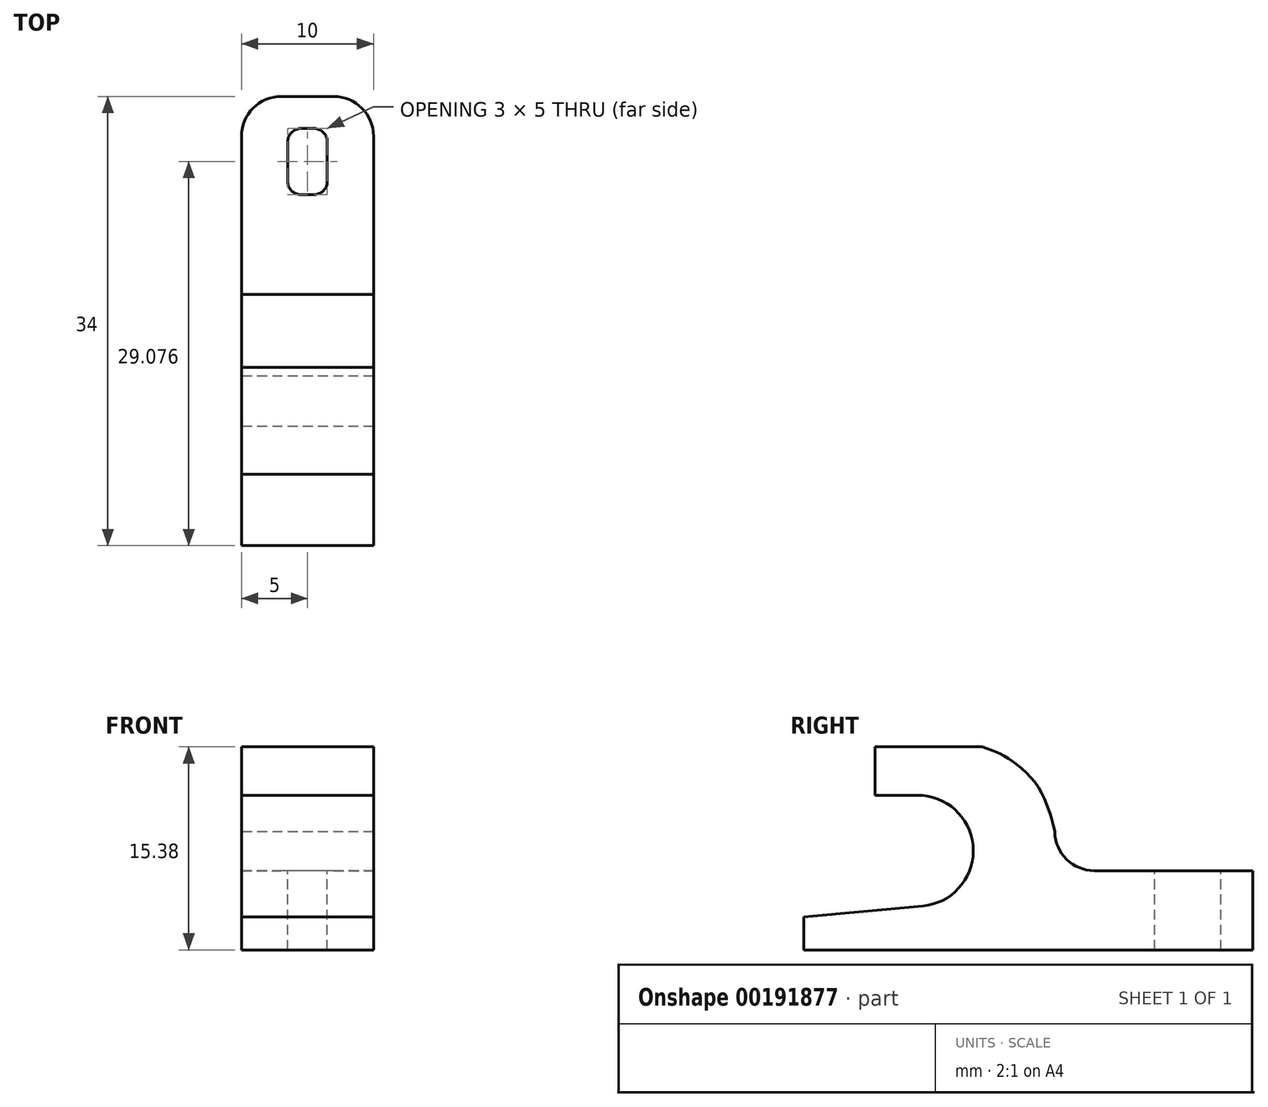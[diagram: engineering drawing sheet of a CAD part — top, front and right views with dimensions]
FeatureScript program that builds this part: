
annotation { "Feature Type Name" : "Feature", "Feature Type Description" : "" }
export const myFeature = defineFeature(function(context is Context, id is Id, definition is map)
    precondition{}
    {
        {
            var Q0;
            Q0=qCreatedBy(makeId("Right.planeOp"),FACE);
            var sketch = newSketch(context, id + "F0", { "sketchPlane" : qUnion([Q0])});
            skLineSegment(sketch, "E0", {"start": v(0, 0) * mm, "end": v(34, 0) * mm});
            skLineSegment(sketch, "E1", {"start": v(34, 0) * mm, "end": v(34, 6) * mm});
            skLineSegment(sketch, "E2", {"start": v(34, 6) * mm, "end": v(19, 6) * mm});
            skLineSegment(sketch, "E3", {"start": v(19, 6) * mm, "end": v(19, 8.93) * mm});
            skLineSegment(sketch, "E4", {"start": v(0, 2.5) * mm, "end": v(0, 0) * mm});
            skLineSegment(sketch, "E5", {"start": v(0, 2.5) * mm, "end": v(9, 3.32) * mm});
            skArc(sketch, "E6", {"start": v(9, 3.32) * mm, "mid": v(12.83, 7.5) * mm, "end": v(9, 11.7) * mm});
            skLineSegment(sketch, "E7", {"start": v(9, 11.7) * mm, "end": v(5.4, 11.7) * mm});
            skLineSegment(sketch, "E8", {"start": v(5.4, 11.7) * mm, "end": v(5.4, 13.28) * mm});
            skLineSegment(sketch, "E9", {"start": v(5.4, 13.28) * mm, "end": v(5.4, 15.38) * mm});
            skLineSegment(sketch, "E10", {"start": v(5.4, 15.38) * mm, "end": v(13.5, 15.38) * mm});
            skFitSpline(sketch, "E11", {"points": [v(13.5, 15.38) * mm, v(15.35, 14.6) * mm, v(17.58, 12.58) * mm, v(18.76, 9.98) * mm, v(19, 8.93) * mm, v(19.4, 7.6) * mm, v(20.08, 8.62) * mm, v(20.9, 12) * mm, v(21.25, 17.14) * mm, v(15.66, 18.14) * mm, v(13.29, 16.85) * mm, v(13.45, 16.25) * mm, v(11.41, 16.25) * mm, v(13.5, 15.38) * mm]});
            skPoint(sketch, "E12.start.orphan", {"position": v(19, 15.38) * mm});
            skPoint(sketch, "E13.orphan", {"position": v(19, 13.28) * mm});
            skPoint(sketch, "E14.end.orphan", {"position": v(9, 13.28) * mm});
            skSolve(sketch);
        }
        {
            var Q0;
            Q0=makeQuery(id+"F0.imprint","IMPRINT",FACE,{"disambiguationData":[TD([[makeQuery(id+"F0.imprint","IMPRINT",EDGE,{"derivedFrom":sQuery(id+"F0.wireOp",EDGE,"E0")}),1.0]])]});
            extrude(context, id + "F1", {"entities" : qUnion([Q0]), "depth" : 10 * mm});
        }
        {
            var Q0;
            Q0=makeQuery(id+"F1.opExtrude","SWEPT_EDGE",EDGE,{"disambiguationData":[OSD([sQuery(id+"F0.wireOp",EDGE,"E2"),sQuery(id+"F0.wireOp",EDGE,"E3")])]});
            var Q1;
            Q1=makeQuery(id+"F1.opExtrude","CAP_EDGE",EDGE,{"disambiguationData":[OSD([sQuery(id+"F0.wireOp",EDGE,"E1")])],"isStart":false});
            var Q2;
            Q2=makeQuery(id+"F1.opExtrude","CAP_EDGE",EDGE,{"disambiguationData":[OSD([sQuery(id+"F0.wireOp",EDGE,"E1")])],"isStart":true});
            fillet(context, id + "F2", {"entities" : qUnion([Q0, Q1, Q2]), "radius" : 3 * mm, "tangentPropagation" : true, "allowEdgeOverflow" : false});
        }
        {
            var Q0;
            Q0=makeQuery(id+"F1.opExtrude","SWEPT_FACE",FACE,{"disambiguationData":[OSD([sQuery(id+"F0.wireOp",EDGE,"E2")])]});
            var sketch = newSketch(context, id + "F3", { "sketchPlane" : qUnion([Q0])});
            skLineSegment(sketch, "E15.bottom", {"start": v(6.5, 26.58) * mm, "end": v(3.5, 26.58) * mm});
            skLineSegment(sketch, "E15.top", {"start": v(6.5, 31.58) * mm, "end": v(3.5, 31.58) * mm});
            skLineSegment(sketch, "E15.left", {"start": v(6.5, 26.58) * mm, "end": v(6.5, 31.58) * mm});
            skLineSegment(sketch, "E15.right", {"start": v(3.5, 26.58) * mm, "end": v(3.5, 31.58) * mm});
            skPoint(sketch, "E15.middle", {"position": v(5, 29.08) * mm});
            skPoint(sketch, "E15.middle.positionSnap0", {"position": v(5, 34) * mm});
            skPoint(sketch, "E15.centerSnap0", {"position": v(5, 34) * mm});
            skSolve(sketch);
        }
        {
            var Q0;
            Q0=makeQuery(id+"F3.imprint","IMPRINT",FACE,{"disambiguationData":[TD([[makeQuery(id+"F3.imprint","IMPRINT",EDGE,{"derivedFrom":sQuery(id+"F3.wireOp",EDGE,"E15.bottom")}),-1.0]])]});
            extrude(context, id + "F4", {"entities" : qUnion([Q0]), "operationType" : NewBodyOperationType.REMOVE, "oppositeDirection" : true, "depth" : 25 * mm});
        }
        {
            var Q0;
            Q0=makeQuery(id+"F4.boolean.opBoolean","COPY",EDGE,{"derivedFrom":makeQuery(id+"F4.opExtrude","SWEPT_EDGE",EDGE,{"disambiguationData":[OSD([sQuery(id+"F3.wireOp",EDGE,"E15.bottom"),sQuery(id+"F3.wireOp",EDGE,"E15.right")])]})});
            var Q1;
            Q1=makeQuery(id+"F4.boolean.opBoolean","COPY",EDGE,{"derivedFrom":makeQuery(id+"F4.opExtrude","SWEPT_EDGE",EDGE,{"disambiguationData":[OSD([sQuery(id+"F3.wireOp",EDGE,"E15.top"),sQuery(id+"F3.wireOp",EDGE,"E15.right")])]})});
            var Q2;
            Q2=makeQuery(id+"F4.boolean.opBoolean","COPY",EDGE,{"derivedFrom":makeQuery(id+"F4.opExtrude","SWEPT_EDGE",EDGE,{"disambiguationData":[OSD([sQuery(id+"F3.wireOp",EDGE,"E15.bottom"),sQuery(id+"F3.wireOp",EDGE,"E15.left")])]})});
            var Q3;
            Q3=makeQuery(id+"F4.boolean.opBoolean","COPY",EDGE,{"derivedFrom":makeQuery(id+"F4.opExtrude","SWEPT_EDGE",EDGE,{"disambiguationData":[OSD([sQuery(id+"F3.wireOp",EDGE,"E15.top"),sQuery(id+"F3.wireOp",EDGE,"E15.left")])]})});
            fillet(context, id + "F5", {"entities" : qUnion([Q0, Q1, Q2, Q3]), "radius" : 1 * mm, "tangentPropagation" : true, "allowEdgeOverflow" : false});
        }
    });
